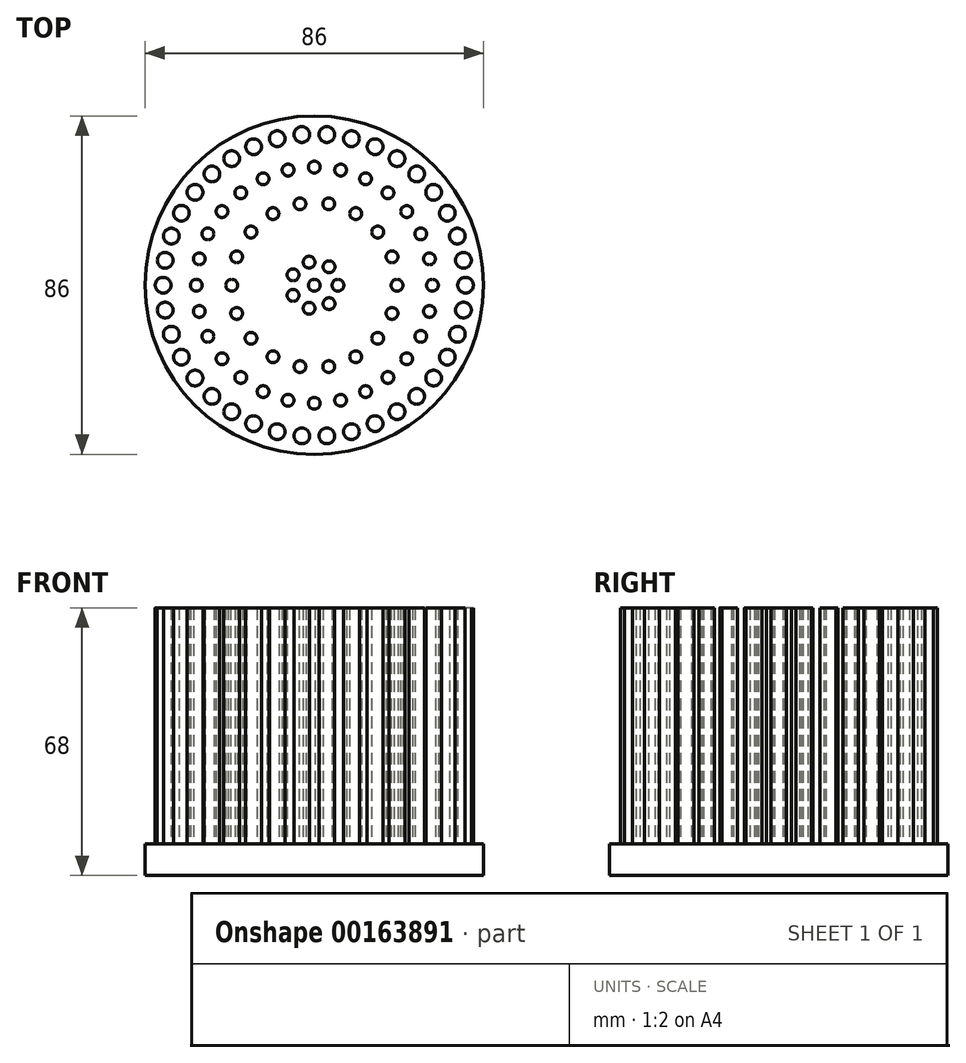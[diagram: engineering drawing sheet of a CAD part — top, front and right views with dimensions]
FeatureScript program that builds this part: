
annotation { "Feature Type Name" : "Feature", "Feature Type Description" : "" }
export const myFeature = defineFeature(function(context is Context, id is Id, definition is map)
    precondition{}
    {
        {
            assignVariable(context, id + "F0", {"name" : "Base", "anyValue" : 8});
        }
        {
            assignVariable(context, id + "F1", {"name" : "Fin_Height", "anyValue" : 60});
        }
        {
            var Q0;
            Q0=qCreatedBy(makeId("Top.planeOp"),FACE);
            var sketch = newSketch(context, id + "F2", { "sketchPlane" : qUnion([Q0])});
            skCircle(sketch, "E0", {"center": v(0, 0) * mm, "radius": 43 * mm});
            skSolve(sketch);
        }
        {
            var Q0;
            Q0=makeQuery(id+"F2.imprint","IMPRINT",FACE,{"disambiguationData":[TD([[makeQuery(id+"F2.imprint","IMPRINT",EDGE,{"derivedFrom":sQuery(id+"F2.wireOp",EDGE,"E0")}),1.0]])]});
            extrude(context, id + "F3", {"entities" : qUnion([Q0]), "depth" : (getVariable(context, 'Base')) * mm});
        }
        {
            var Q0;
            Q0=makeQuery(id+"F3.opExtrude","CAP_FACE",FACE,{"disambiguationData":[OSD([sQuery(id+"F2.wireOp",EDGE,"E0")])],"isStart":false});
            var sketch = newSketch(context, id + "F4", { "sketchPlane" : qUnion([Q0])});
            skCircle(sketch, "E1", {"center": v(0, 0) * mm, "radius": 1.5 * mm});
            skCircle(sketch, "E2", {"center": v(6, 0) * mm, "radius": 1.5 * mm});
            skCircle(sketch, "E3", {"center": v(21, 0) * mm, "radius": 1.5 * mm});
            skCircle(sketch, "E4", {"center": v(38.4, 0) * mm, "radius": 2 * mm});
            skCircle(sketch, "E5.1.0", {"center": v(3.74, 4.7) * mm, "radius": 1.5 * mm});
            skCircle(sketch, "E5.2.0", {"center": v(-1.34, 5.85) * mm, "radius": 1.5 * mm});
            skCircle(sketch, "E5.3.0", {"center": v(-5.4, 2.6) * mm, "radius": 1.5 * mm});
            skCircle(sketch, "E5.4.0", {"center": v(-5.4, -2.6) * mm, "radius": 1.5 * mm});
            skCircle(sketch, "E5.5.0", {"center": v(-1.34, -5.85) * mm, "radius": 1.5 * mm});
            skCircle(sketch, "E5.6.0", {"center": v(3.74, -4.7) * mm, "radius": 1.5 * mm});
            skCircle(sketch, "E6.1.0", {"center": v(19.73, 7.18) * mm, "radius": 1.5 * mm});
            skCircle(sketch, "E6.2.0", {"center": v(16.09, 13.5) * mm, "radius": 1.5 * mm});
            skCircle(sketch, "E6.3.0", {"center": v(10.5, 18.19) * mm, "radius": 1.5 * mm});
            skCircle(sketch, "E6.4.0", {"center": v(3.65, 20.68) * mm, "radius": 1.5 * mm});
            skCircle(sketch, "E6.5.0", {"center": v(-3.65, 20.68) * mm, "radius": 1.5 * mm});
            skCircle(sketch, "E6.6.0", {"center": v(-10.5, 18.19) * mm, "radius": 1.5 * mm});
            skCircle(sketch, "E6.7.0", {"center": v(-16.09, 13.5) * mm, "radius": 1.5 * mm});
            skCircle(sketch, "E6.8.0", {"center": v(-19.73, 7.18) * mm, "radius": 1.5 * mm});
            skCircle(sketch, "E6.9.0", {"center": v(-21, 0) * mm, "radius": 1.5 * mm});
            skCircle(sketch, "E6.10.0", {"center": v(-19.73, -7.18) * mm, "radius": 1.5 * mm});
            skCircle(sketch, "E6.11.0", {"center": v(-16.09, -13.5) * mm, "radius": 1.5 * mm});
            skCircle(sketch, "E6.12.0", {"center": v(-10.5, -18.19) * mm, "radius": 1.5 * mm});
            skCircle(sketch, "E6.13.0", {"center": v(-3.65, -20.68) * mm, "radius": 1.5 * mm});
            skCircle(sketch, "E6.14.0", {"center": v(3.65, -20.68) * mm, "radius": 1.5 * mm});
            skCircle(sketch, "E6.15.0", {"center": v(10.5, -18.19) * mm, "radius": 1.5 * mm});
            skCircle(sketch, "E6.16.0", {"center": v(16.09, -13.5) * mm, "radius": 1.5 * mm});
            skCircle(sketch, "E6.17.0", {"center": v(19.73, -7.18) * mm, "radius": 1.5 * mm});
            skCircle(sketch, "E7", {"center": v(30, 0) * mm, "radius": 1.5 * mm});
            skCircle(sketch, "E8.1.0", {"center": v(29.25, 6.68) * mm, "radius": 1.5 * mm});
            skCircle(sketch, "E8.2.0", {"center": v(27.03, 13.02) * mm, "radius": 1.5 * mm});
            skCircle(sketch, "E8.3.0", {"center": v(23.45, 18.7) * mm, "radius": 1.5 * mm});
            skCircle(sketch, "E8.4.0", {"center": v(18.7, 23.45) * mm, "radius": 1.5 * mm});
            skCircle(sketch, "E8.5.0", {"center": v(13.02, 27.03) * mm, "radius": 1.5 * mm});
            skCircle(sketch, "E8.6.0", {"center": v(6.68, 29.25) * mm, "radius": 1.5 * mm});
            skCircle(sketch, "E8.7.0", {"center": v(0, 30) * mm, "radius": 1.5 * mm});
            skCircle(sketch, "E8.8.0", {"center": v(-6.68, 29.25) * mm, "radius": 1.5 * mm});
            skCircle(sketch, "E8.9.0", {"center": v(-13.02, 27.03) * mm, "radius": 1.5 * mm});
            skCircle(sketch, "E8.10.0", {"center": v(-18.7, 23.45) * mm, "radius": 1.5 * mm});
            skCircle(sketch, "E8.11.0", {"center": v(-23.45, 18.7) * mm, "radius": 1.5 * mm});
            skCircle(sketch, "E8.12.0", {"center": v(-27.03, 13.02) * mm, "radius": 1.5 * mm});
            skCircle(sketch, "E8.13.0", {"center": v(-29.25, 6.68) * mm, "radius": 1.5 * mm});
            skCircle(sketch, "E8.14.0", {"center": v(-30, 0) * mm, "radius": 1.5 * mm});
            skCircle(sketch, "E8.15.0", {"center": v(-29.25, -6.68) * mm, "radius": 1.5 * mm});
            skCircle(sketch, "E8.16.0", {"center": v(-27.03, -13.02) * mm, "radius": 1.5 * mm});
            skCircle(sketch, "E8.17.0", {"center": v(-23.45, -18.7) * mm, "radius": 1.5 * mm});
            skCircle(sketch, "E8.18.0", {"center": v(-18.7, -23.45) * mm, "radius": 1.5 * mm});
            skCircle(sketch, "E8.19.0", {"center": v(-13.02, -27.03) * mm, "radius": 1.5 * mm});
            skCircle(sketch, "E8.20.0", {"center": v(-6.68, -29.25) * mm, "radius": 1.5 * mm});
            skCircle(sketch, "E8.21.0", {"center": v(0, -30) * mm, "radius": 1.5 * mm});
            skCircle(sketch, "E8.22.0", {"center": v(6.68, -29.25) * mm, "radius": 1.5 * mm});
            skCircle(sketch, "E8.23.0", {"center": v(13.02, -27.03) * mm, "radius": 1.5 * mm});
            skCircle(sketch, "E8.24.0", {"center": v(18.7, -23.45) * mm, "radius": 1.5 * mm});
            skCircle(sketch, "E8.25.0", {"center": v(23.45, -18.7) * mm, "radius": 1.5 * mm});
            skCircle(sketch, "E8.26.0", {"center": v(27.03, -13.02) * mm, "radius": 1.5 * mm});
            skCircle(sketch, "E8.27.0", {"center": v(29.25, -6.68) * mm, "radius": 1.5 * mm});
            skCircle(sketch, "E9.1.0", {"center": v(37.89, 6.32) * mm, "radius": 2 * mm});
            skCircle(sketch, "E9.2.0", {"center": v(36.33, 12.47) * mm, "radius": 2 * mm});
            skCircle(sketch, "E9.3.0", {"center": v(33.78, 18.28) * mm, "radius": 2 * mm});
            skCircle(sketch, "E9.4.0", {"center": v(30.31, 23.6) * mm, "radius": 2 * mm});
            skCircle(sketch, "E9.5.0", {"center": v(26.01, 28.26) * mm, "radius": 2 * mm});
            skCircle(sketch, "E9.6.0", {"center": v(21, 32.16) * mm, "radius": 2 * mm});
            skCircle(sketch, "E9.7.0", {"center": v(15.43, 35.17) * mm, "radius": 2 * mm});
            skCircle(sketch, "E9.8.0", {"center": v(9.43, 37.23) * mm, "radius": 2 * mm});
            skCircle(sketch, "E9.9.0", {"center": v(3.17, 38.28) * mm, "radius": 2 * mm});
            skCircle(sketch, "E9.10.0", {"center": v(-3.17, 38.28) * mm, "radius": 2 * mm});
            skCircle(sketch, "E9.11.0", {"center": v(-9.43, 37.23) * mm, "radius": 2 * mm});
            skCircle(sketch, "E9.12.0", {"center": v(-15.43, 35.17) * mm, "radius": 2 * mm});
            skCircle(sketch, "E9.13.0", {"center": v(-21, 32.16) * mm, "radius": 2 * mm});
            skCircle(sketch, "E9.14.0", {"center": v(-26.01, 28.26) * mm, "radius": 2 * mm});
            skCircle(sketch, "E9.15.0", {"center": v(-30.31, 23.6) * mm, "radius": 2 * mm});
            skCircle(sketch, "E9.16.0", {"center": v(-33.78, 18.28) * mm, "radius": 2 * mm});
            skCircle(sketch, "E9.17.0", {"center": v(-36.33, 12.47) * mm, "radius": 2 * mm});
            skCircle(sketch, "E9.18.0", {"center": v(-37.89, 6.32) * mm, "radius": 2 * mm});
            skCircle(sketch, "E9.19.0", {"center": v(-38.4, 0) * mm, "radius": 2 * mm});
            skCircle(sketch, "E9.20.0", {"center": v(-37.89, -6.32) * mm, "radius": 2 * mm});
            skCircle(sketch, "E9.21.0", {"center": v(-36.33, -12.47) * mm, "radius": 2 * mm});
            skCircle(sketch, "E9.22.0", {"center": v(-33.78, -18.28) * mm, "radius": 2 * mm});
            skCircle(sketch, "E9.23.0", {"center": v(-30.31, -23.6) * mm, "radius": 2 * mm});
            skCircle(sketch, "E9.24.0", {"center": v(-26.01, -28.26) * mm, "radius": 2 * mm});
            skCircle(sketch, "E9.25.0", {"center": v(-21, -32.16) * mm, "radius": 2 * mm});
            skCircle(sketch, "E9.26.0", {"center": v(-15.43, -35.17) * mm, "radius": 2 * mm});
            skCircle(sketch, "E9.27.0", {"center": v(-9.43, -37.23) * mm, "radius": 2 * mm});
            skCircle(sketch, "E9.28.0", {"center": v(-3.17, -38.28) * mm, "radius": 2 * mm});
            skCircle(sketch, "E9.29.0", {"center": v(3.17, -38.28) * mm, "radius": 2 * mm});
            skCircle(sketch, "E9.30.0", {"center": v(9.43, -37.23) * mm, "radius": 2 * mm});
            skCircle(sketch, "E9.31.0", {"center": v(15.43, -35.17) * mm, "radius": 2 * mm});
            skCircle(sketch, "E9.32.0", {"center": v(21, -32.16) * mm, "radius": 2 * mm});
            skCircle(sketch, "E9.33.0", {"center": v(26.01, -28.26) * mm, "radius": 2 * mm});
            skCircle(sketch, "E9.34.0", {"center": v(30.31, -23.6) * mm, "radius": 2 * mm});
            skCircle(sketch, "E9.35.0", {"center": v(33.78, -18.28) * mm, "radius": 2 * mm});
            skCircle(sketch, "E9.36.0", {"center": v(36.33, -12.47) * mm, "radius": 2 * mm});
            skCircle(sketch, "E9.37.0", {"center": v(37.89, -6.32) * mm, "radius": 2 * mm});
            skSolve(sketch);
        }
        {
            var Q0;
            Q0 = qSketchRegion(id + "F4", true);
            extrude(context, id + "F5", {"entities" : qUnion([Q0]), "operationType" : NewBodyOperationType.ADD, "depth" : (getVariable(context, 'Fin_Height')) * mm});
        }
    });
